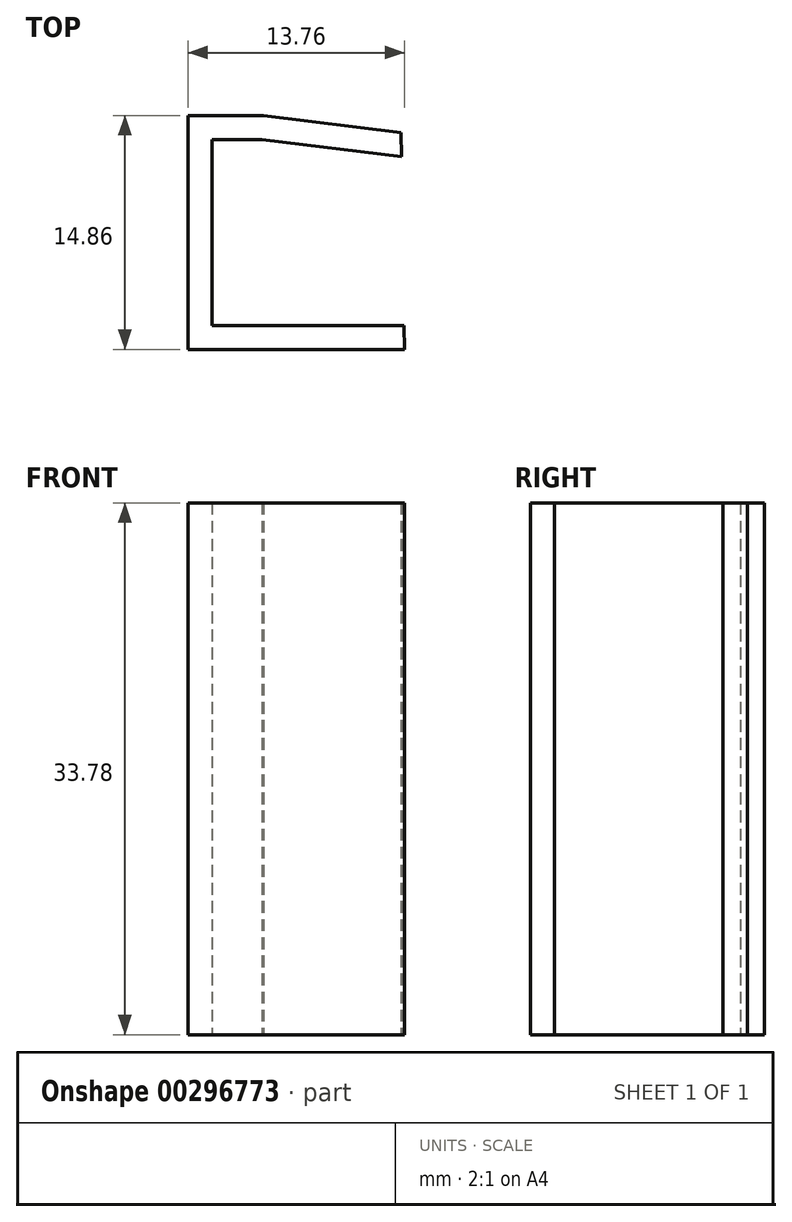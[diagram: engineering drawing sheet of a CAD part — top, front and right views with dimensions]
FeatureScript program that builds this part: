
annotation { "Feature Type Name" : "Feature", "Feature Type Description" : "" }
export const myFeature = defineFeature(function(context is Context, id is Id, definition is map)
    precondition{}
    {
        {
            var Q0;
            Q0=qCreatedBy(makeId("Top.planeOp"),FACE);
            var sketch = newSketch(context, id + "F0", { "sketchPlane" : qUnion([Q0])});
            skLineSegment(sketch, "E0", {"start": v(5.23, -7.7) * mm, "end": v(-6.97, -7.7) * mm});
            skLineSegment(sketch, "E1", {"start": v(-6.97, -7.7) * mm, "end": v(-6.97, 4.1) * mm});
            skLineSegment(sketch, "E2", {"start": v(-6.97, 4.1) * mm, "end": v(-3.8, 4.1) * mm});
            skLineSegment(sketch, "E3", {"start": v(-3.8, 4.1) * mm, "end": v(5.06, 3) * mm});
            skLineSegment(sketch, "E4.0", {"start": v(5.26, -9.23) * mm, "end": v(-8.5, -9.23) * mm});
            skLineSegment(sketch, "E5.0", {"start": v(-8.5, -9.23) * mm, "end": v(-8.5, 4.17) * mm});
            skLineSegment(sketch, "E6.0", {"start": v(-7.44, 5.63) * mm, "end": v(-4.27, 5.63) * mm});
            skLineSegment(sketch, "E7.0", {"start": v(-3.7, 5.63) * mm, "end": v(5.03, 4.54) * mm});
            skLineSegment(sketch, "E8", {"start": v(5.26, -9.23) * mm, "end": v(5.23, -7.7) * mm});
            skLineSegment(sketch, "E9", {"start": v(-4.27, 5.63) * mm, "end": v(-3.7, 5.63) * mm});
            skLineSegment(sketch, "E10", {"start": v(-8.5, 4.17) * mm, "end": v(-8.5, 5.63) * mm});
            skLineSegment(sketch, "E11.trimOffspring", {"start": v(5.06, 3) * mm, "end": v(5.03, 4.54) * mm});
            skLineSegment(sketch, "E12", {"start": v(-8.5, 5.63) * mm, "end": v(-7.44, 5.63) * mm});
            skSolve(sketch);
        }
        {
            var Q0;
            Q0=makeQuery(id+"F0.imprint","IMPRINT",FACE,{"disambiguationData":[TD([[makeQuery(id+"F0.imprint","IMPRINT",EDGE,{"derivedFrom":sQuery(id+"F0.wireOp",EDGE,"E0")}),1.0]])]});
            extrude(context, id + "F1", {"entities" : qUnion([Q0]), "depth" : 33.78 * mm});
        }
        {
            var Q0;
            Q0=makeQuery(id+"F1.opExtrude","SWEPT_FACE",FACE,{"disambiguationData":[OSD([sQuery(id+"F0.wireOp",EDGE,"E4.0")])]});
            var sketch = newSketch(context, id + "F2", { "sketchPlane" : qUnion([Q0])});
            skLineSegment(sketch, "E13", {"start": v(-8.5, 0) * mm, "end": v(-8.5, 33.78) * mm});
            skLineSegment(sketch, "E14", {"start": v(-8.5, 33.78) * mm, "end": v(-41.32, 33.78) * mm});
            skSolve(sketch);
        }
    });
